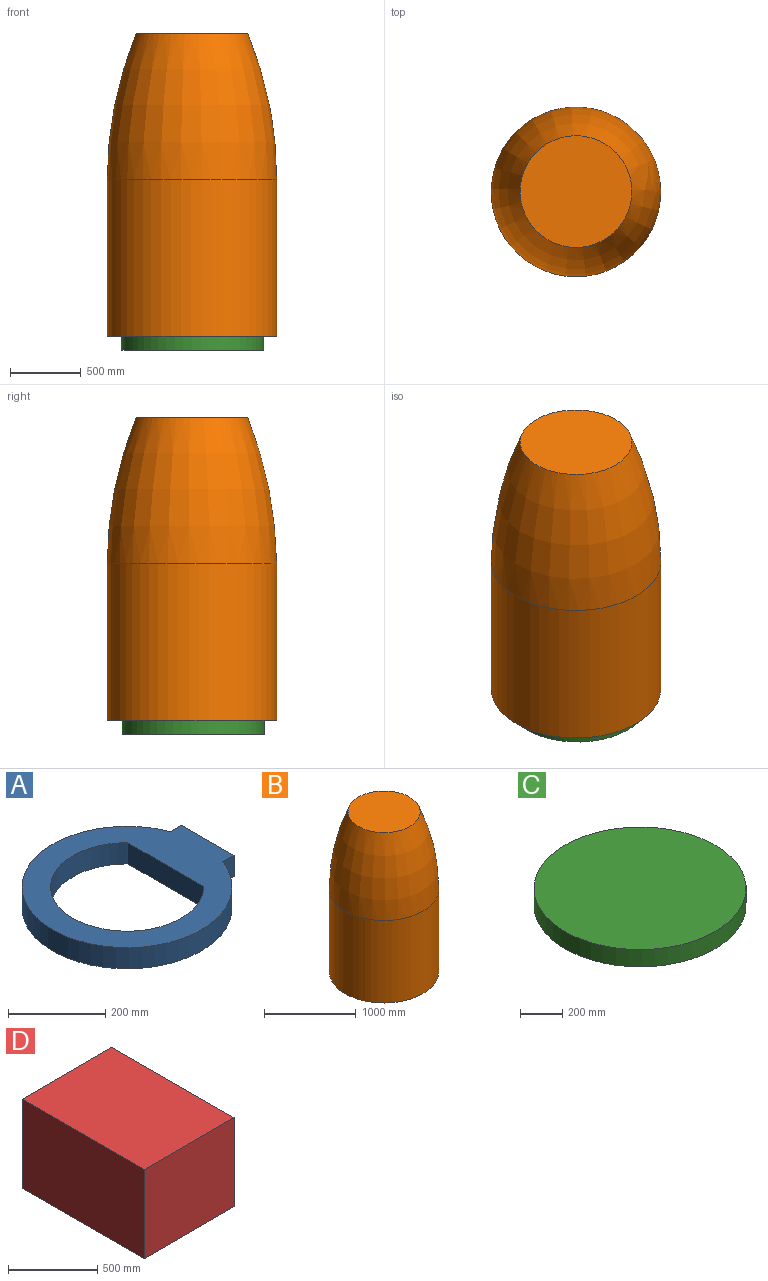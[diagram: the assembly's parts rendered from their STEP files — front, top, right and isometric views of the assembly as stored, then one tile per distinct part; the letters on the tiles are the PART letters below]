
ASSEMBLY  parts=4 mates=6
PART A: 8 faces, bbox 451.1x432.3x53.3 mm
  f0: plane 53.34x32.67mm, normal (0,1,0), area 1742.8mm2, adj f1,f5,f6,f7
  f1: cylinder r=216.15mm len=432.31mm, axis (0,0,-1), area 64135.4mm2, adj f0,f2,f6,f7
  f2: plane 53.34x32.67mm, normal (0,-1,0), area 1742.8mm2, adj f1,f5,f6,f7
  f3: cylinder r=157.61mm len=315.21mm, axis (0,0,-1), area 39779.2mm2, adj f4,f6,f7
  f4: plane 220.72x53.34mm, normal (-1,0,0), area 11772.9mm2, adj f3,f6,f7
  f5: plane 152.4x53.34mm, normal (1,0,0), area 8129mm2, adj f0,f2,f6,f7
  f6: plane 451.1x432.31mm, normal (0,0,1), area 79156.7mm2, adj f0,f1,f2,f3,f4,f5
  f7: plane 451.1x432.31mm, normal (0,0,-1), area 79156.7mm2, adj f0,f1,f2,f3,f4,f5
PART B: 4 faces, bbox 1194x1194x2129 mm
  f0: plane 787x787mm, normal (0,0,1), area 486451.3mm2, adj f1
  f1: revolved ~1194x1194mm, area 3509350.9mm2, adj f0,f2
  f2: cylinder r=597mm len=1194mm, axis (0,0,1), area 4126167.8mm2, adj f1,f3
  f3: plane 1194x1194mm, normal (0,0,-1), area 1119691.9mm2, adj f2
PART C: 3 faces, bbox 1003x1003x100 mm
  f0: cylinder r=501.5mm len=1003mm, axis (0,0,-1), area 315101.7mm2, adj f1,f2
  f1: plane 1003x1003mm, normal (0,0,1), area 790117.6mm2, adj f0
  f2: plane 1003x1003mm, normal (0,0,-1), area 790117.6mm2, adj f0
PART D: 6 faces, bbox 711x965x610 mm
  f0: plane 965x711mm, normal (0,0,1), area 686115mm2, adj f1,f3,f4,f5
  f1: plane 965x610mm, normal (-1,0,0), area 588650mm2, adj f0,f2,f4,f5
  f2: plane 965x711mm, normal (0,0,-1), area 686115mm2, adj f1,f3,f4,f5
  f3: plane 965x610mm, normal (1,0,0), area 588650mm2, adj f0,f2,f4,f5
  f4: plane 711x610mm, normal (0,1,0), area 433710mm2, adj f0,f1,f2,f3
  f5: plane 711x610mm, normal (0,-1,0), area 433710mm2, adj f0,f1,f2,f3
PLACE A rot(axis=(0,0,-1),67.5deg) t=(-100.05,-936.77,-6316.75)mm
PLACE B rot(axis=(0,0,1),22.5deg) t=(-104,-927.26,-6316.75)mm
PLACE C rot(axis=(0,0,1),22.5deg) t=(-100.05,-936.77,-6416.75)mm
PLACE D rot(axis=(-0.14,0.7,-0.7),164.1deg) t=(-549.21,-781.69,-5298.41)mm
MATE parallel A.f5 <-> D.f0  axis (0.38,-0.92,0) through (-10.06,-1153.8,-6290.08)mm
MATE revolute C.f0 <-> A.f1  axis (0,0,1) through (-100.05,-936.77,-6316.75)mm
MATE cylindrical B.f2 <-> D.f4  axis (0,0,1) through (-104,-927.26,-6316.75)mm
MATE planar A.f6 <-> D.f4  axis (0,0,1) through (-91.88,-956.48,-6263.41)mm
MATE cylindrical A.f7 <-> D.f4  axis (0,0,-1) through (-104,-927.26,-6316.75)mm
MATE planar A.f7 <-> B.f2  axis (0,0,-1) through (47.82,-1094.43,-6316.75)mm
